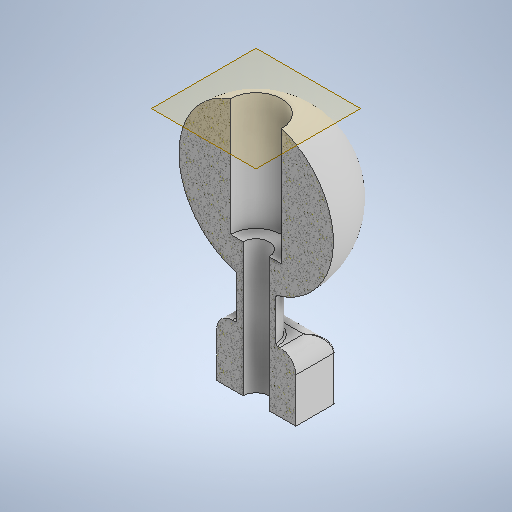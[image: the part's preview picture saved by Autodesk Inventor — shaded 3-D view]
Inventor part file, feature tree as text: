
AUTODESK INVENTOR PART (.ipt)
format: ipt  version: 2025.1 (Build 291241000, 241)  size: 375,808 bytes
history: native  units: mm
features: sketch x5, extrude x4, fillet x4, revolve x1, plane x1
ambient origin geometry x8: Origin, YZ Plane, XZ Plane, XY Plane, X Axis, Y Axis, Z Axis, Center Point
bodies: Volumenkörper1 (feature_tree)
feature tree (15):
  extrude  "Extrusion1"  Depth=6.0mm TaperAngle=0.0deg
  revolve  "Umdrehung1"
  plane  "Arbeitsebene1"
  extrude  "Extrusion5"  Depth=9.75mm
  fillet  "Rundung6"  Radius=9.75mm
  fillet  "Rundung7"  Radius=14.9mm
  fillet  "Rundung8"  [1 undecoded]
  extrude  "Extrusion6"  Depth=5.0mm
  fillet  "Rundung9"  Radius=5.0mm
  extrude  "Extrusion7"  Depth=10.0mm
  sketch  "Skizze1"  dims[d0=5.0mm d1=6.0mm d2=0.0mm]
  sketch  "Skizze3"  dims[d6=19.5mm d7=9.75mm d8=9.75mm d10=14.9mm d11=0.0mm]
  sketch  "Skizze6"  dims[d12=90.0deg d21=5.0mm d22=5.0mm]
  sketch  "Skizze7"  dims[d23=10.0mm d24=5.0mm]
  sketch  "Skizze8"  dims[d25=7.6mm d26=0.0mm d30=2.0mm d31=0.2mm d32=0.2mm d33=3.3mm d34=1.0mm d35=0.0mm d36=0.2mm d37=6.5mm d38=15.4mm d39=0.0mm]
note: 1 required parameter value undecoded (feature->parameter linkage not recoverable at this tier; creation-order binding heuristic only, values carry confidence <= 0.55)
